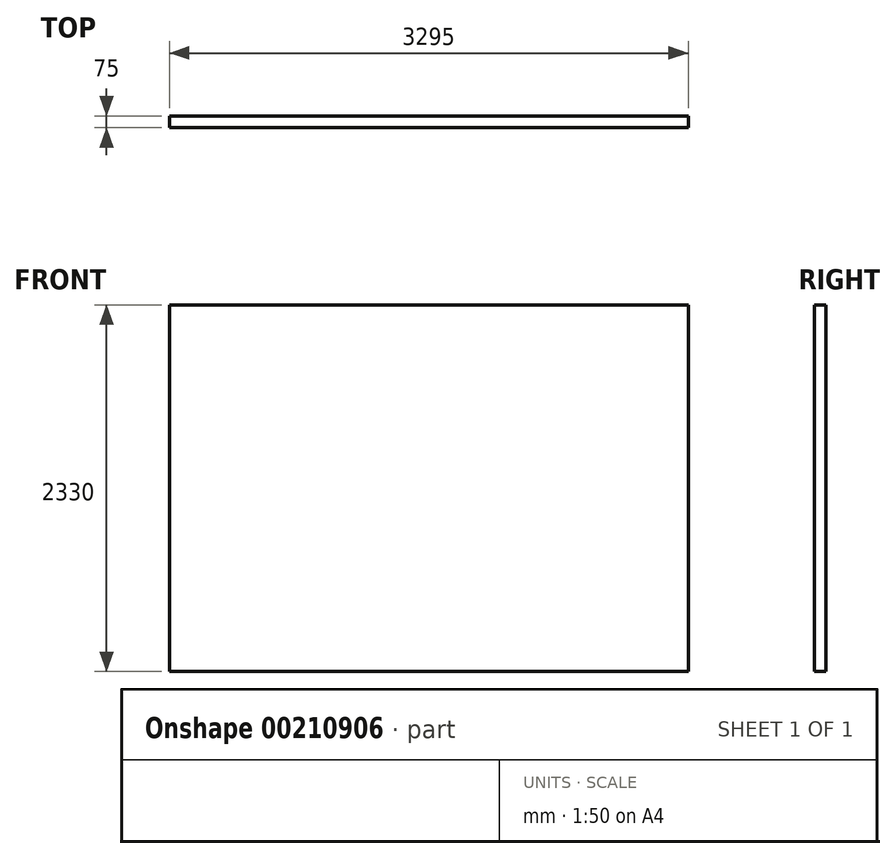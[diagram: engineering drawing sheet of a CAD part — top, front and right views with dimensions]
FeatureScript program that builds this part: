
annotation { "Feature Type Name" : "Feature", "Feature Type Description" : "" }
export const myFeature = defineFeature(function(context is Context, id is Id, definition is map)
    precondition{}
    {
        {
            var Q0;
            Q0=qCreatedBy(makeId("Front.planeOp"),FACE);
            var sketch = newSketch(context, id + "F0", { "sketchPlane" : qUnion([Q0])});
            skLineSegment(sketch, "E0.bottom", {"start": v(0, 0) * mm, "end": v(3295, 0) * mm});
            skLineSegment(sketch, "E0.right", {"start": v(3295, 0) * mm, "end": v(3295, 2330) * mm});
            skLineSegment(sketch, "E1", {"start": v(0, 0) * mm, "end": v(0, 2330) * mm});
            skLineSegment(sketch, "E2", {"start": v(0, 2330) * mm, "end": v(3295, 2330) * mm});
            skSolve(sketch);
        }
        {
            var Q0;
            Q0=makeQuery(id+"F0.imprint","IMPRINT",FACE,{"disambiguationData":[TD([[makeQuery(id+"F0.imprint","IMPRINT",EDGE,{"derivedFrom":sQuery(id+"F0.wireOp",EDGE,"E0.bottom")}),1.0]])]});
            extrude(context, id + "F1", {"entities" : qUnion([Q0]), "depth" : 75 * mm});
        }
    });
